# Revit family: 799090001_Válvula Duplex Orinal
name_source: partatom
category: Generic Models
units: mm (PartAtom-declared; Revit-internal decimal feet)

## family parameters
Always vertical = Yes
Can host rebar = No
Cut with Voids When Loaded = No
Part Type = Normal
Room Calculation Point = No
Round Connector Dimension = Use Diameter
Shared = No
Work Plane-Based = No

## types (1)
- 799090001_Válvula Duplex Orinal
    Acabado = Corona_Cromado
    Alto = 17 cm
    Ancho = 17 cm
    Capacidad de flujo = 0.43 l/m a 50 PSI
    Colección = Duplex
    Consumo de agua = 0.5 lt
    Creado por = IDD
    Description = El aliado perfecto para las necesidades de las instituciones de alto tráfico porque su diseño ofrece un óptimo funcionamiento y durabilidad debido a suscaracterísticas antivandálicas. Adquiere ahora la válvula de descarga de sensor electrónica y descarga de agua variable según presión. ¡Toma la decisión ahora!
    Fecha de creación = 5/10/2020
    Garantías de otros componentes = 1 año en acabados y elementos electrónicos
    Incluye = Válvula, sensor
    Largo = 6.3 cm
    Línea = Empotrar
    Material = Corona_Metal
    No incluye = Batería de 9 V para sistema de respaldo
    Productos compatibles = Orinales Institucionales Corona
    Rango de presión de agua = Entre 20 y 80 PSI
    Resistencia = Resistente a la corrosión, pelado y decoloración por agua
    Sistema antivandálic = Producto que dificulta las acciones vandálicas
    Sistema de accionamiento = Sensor push
    Tipo de instalación = A pared
    URL = https://corona.co
    Uso = Institucional

## geometry (parser evidence)
native form markers: Sweep x2
no freeform markers — native parametric forms only
